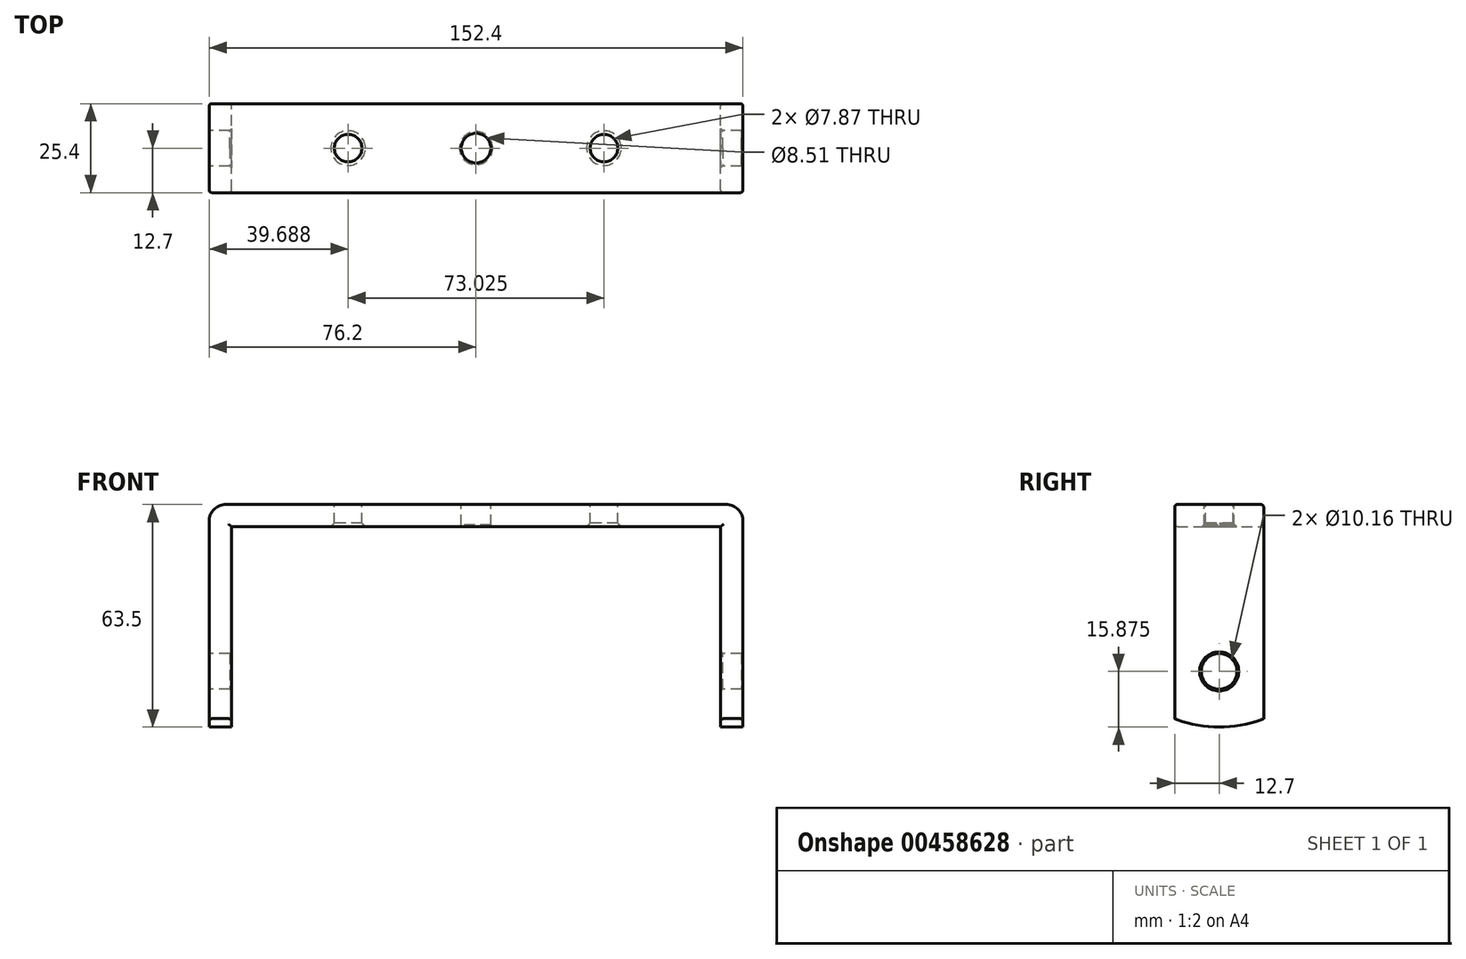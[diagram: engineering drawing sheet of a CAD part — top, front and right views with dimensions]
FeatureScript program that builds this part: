
annotation { "Feature Type Name" : "Feature", "Feature Type Description" : "" }
export const myFeature = defineFeature(function(context is Context, id is Id, definition is map)
    precondition{}
    {
        {
            var Q0;
            Q0=qCreatedBy(makeId("Front.planeOp"),FACE);
            var sketch = newSketch(context, id + "F0", { "sketchPlane" : qUnion([Q0])});
            skLineSegment(sketch, "E0", {"start": v(-69.85, 0) * mm, "end": v(0, 0) * mm});
            skLineSegment(sketch, "E1", {"start": v(-69.85, 0) * mm, "end": v(-69.85, -57.15) * mm});
            skLineSegment(sketch, "E2", {"start": v(0, 0) * mm, "end": v(0, -18.19) * mm, "construction": true});
            skLineSegment(sketch, "E3", {"start": v(-69.85, -57.15) * mm, "end": v(-76.2, -57.15) * mm});
            skLineSegment(sketch, "E4", {"start": v(-76.2, -57.15) * mm, "end": v(-76.2, 6.35) * mm});
            skLineSegment(sketch, "E5", {"start": v(-76.2, 6.35) * mm, "end": v(0, 6.35) * mm});
            skPoint(sketch, "E6.orphan", {"position": v(-69.85, 6.35) * mm});
            skPoint(sketch, "E7.orphan", {"position": v(-76.2, 0) * mm});
            skLineSegment(sketch, "E8.MirrorCS", {"start": v(-69.85, 12.7) * mm, "end": v(0, 12.7) * mm});
            skLineSegment(sketch, "E9.MirrorCS", {"start": v(76.2, 6.35) * mm, "end": v(0, 6.35) * mm});
            skLineSegment(sketch, "E10.MirrorCS", {"start": v(69.85, 0) * mm, "end": v(0, 0) * mm});
            skLineSegment(sketch, "E11.MirrorCS", {"start": v(69.85, 0) * mm, "end": v(69.85, -57.15) * mm});
            skLineSegment(sketch, "E12.MirrorCS", {"start": v(69.85, -57.15) * mm, "end": v(76.2, -57.15) * mm});
            skLineSegment(sketch, "E13.MirrorCS", {"start": v(76.2, -57.15) * mm, "end": v(76.2, 6.35) * mm});
            skSolve(sketch);
        }
        {
            var Q0;
            Q0=makeQuery(id+"F0.imprint","IMPRINT",FACE,{"disambiguationData":[TD([[makeQuery(id+"F0.imprint","IMPRINT",EDGE,{"derivedFrom":sQuery(id+"F0.wireOp",EDGE,"E0")}),1.0]])]});
            extrude(context, id + "F1", {"entities" : qUnion([Q0]), "depth" : 25.4 * mm});
        }
        {
            var Q0;
            Q0=makeQuery(id+"F1.opExtrude","SWEPT_FACE",FACE,{"disambiguationData":[OSD([sQuery(id+"F0.wireOp",EDGE,"E4")])]});
            var sketch = newSketch(context, id + "F2", { "sketchPlane" : qUnion([Q0])});
            skLineSegment(sketch, "E14.0", {"start": v(25.4, 0) * mm, "end": v(0, 0) * mm});
            skCircle(sketch, "E15", {"center": v(12.7, -41.28) * mm, "radius": 5.08 * mm});
            skPoint(sketch, "E15.centerSnap0", {"position": v(12.7, 0) * mm});
            skArc(sketch, "E16", {"start": v(0, -54.76) * mm, "mid": v(12.7, -57.15) * mm, "end": v(25.4, -54.76) * mm});
            skPoint(sketch, "E16.centerSnap0", {"position": v(12.7, -57.15) * mm});
            skLineSegment(sketch, "E17.0", {"start": v(25.4, -57.15) * mm, "end": v(25.4, -54.76) * mm});
            skLineSegment(sketch, "E17.1", {"start": v(25.4, -57.15) * mm, "end": v(0, -57.15) * mm});
            skLineSegment(sketch, "E17.2", {"start": v(0, -57.15) * mm, "end": v(0, -54.76) * mm});
            skLineSegment(sketch, "E18.trimOffspring", {"start": v(0, 0) * mm, "end": v(0, 6.35) * mm});
            skLineSegment(sketch, "E19.trimOffspring", {"start": v(25.4, 0) * mm, "end": v(25.4, 6.35) * mm});
            skSolve(sketch);
        }
        {
            var Q0;
            Q0 = qSketchRegion(id + "F2", true);
            extrude(context, id + "F3", {"entities" : qUnion([Q0]), "operationType" : NewBodyOperationType.REMOVE, "endBound" : BoundingType.THROUGH_ALL, "oppositeDirection" : true, "depth" : 25.4 * mm});
        }
        {
            var Q0;
            Q0=makeQuery(id+"F1.opExtrude","SWEPT_FACE",FACE,{"disambiguationData":[OSD([sQuery(id+"F0.wireOp",EDGE,"E5"),sQuery(id+"F0.wireOp",EDGE,"E9.MirrorCS")])]});
            var sketch = newSketch(context, id + "F4", { "sketchPlane" : qUnion([Q0])});
            skLineSegment(sketch, "E20.0", {"start": v(76.2, 0) * mm, "end": v(-76.2, 0) * mm, "construction": true});
            skLineSegment(sketch, "E20.1", {"start": v(-76.2, -25.4) * mm, "end": v(-76.2, 0) * mm, "construction": true});
            skLineSegment(sketch, "E20.2", {"start": v(76.2, -25.4) * mm, "end": v(-76.2, -25.4) * mm, "construction": true});
            skLineSegment(sketch, "E20.3", {"start": v(76.2, -25.4) * mm, "end": v(76.2, 0) * mm, "construction": true});
            skCircle(sketch, "E21", {"center": v(-36.51, -12.7) * mm, "radius": 3.94 * mm});
            skPoint(sketch, "E21.centerSnap0", {"position": v(-76.2, -12.7) * mm});
            skCircle(sketch, "E22", {"center": v(0, -12.7) * mm, "radius": 4.25 * mm});
            skLineSegment(sketch, "E23", {"start": v(0, 0) * mm, "end": v(0, -25.4) * mm, "construction": true});
            skCircle(sketch, "E24.MirrorC", {"center": v(36.51, -12.7) * mm, "radius": 3.94 * mm});
            skSolve(sketch);
        }
        {
            var Q0;
            Q0 = qSketchRegion(id + "F4", true);
            extrude(context, id + "F5", {"entities" : qUnion([Q0]), "operationType" : NewBodyOperationType.REMOVE, "endBound" : BoundingType.THROUGH_ALL, "oppositeDirection" : true, "depth" : 25.4 * mm});
        }
        {
            var Q0;
            Q0=makeQuery(id+"F5.boolean.opBoolean","COPY",EDGE,{"derivedFrom":makeQuery(id+"F5.opExtrude","CAP_EDGE",EDGE,{"disambiguationData":[OSD([sQuery(id+"F4.wireOp",EDGE,"E21")])],"isStart":true})});
            var Q1;
            Q1=makeQuery(id+"F5.boolean.opBoolean","COPY",EDGE,{"derivedFrom":makeQuery(id+"F5.opExtrude","CAP_EDGE",EDGE,{"disambiguationData":[OSD([sQuery(id+"F4.wireOp",EDGE,"E24.MirrorC")])],"isStart":true})});
            var Q2;
            Q2=makeQuery(id+"F5.boolean.opBoolean","INTERSECT",EDGE,{"derivedFrom":[makeQuery(id+"F1.opExtrude","SWEPT_FACE",FACE,{"disambiguationData":[OSD([sQuery(id+"F0.wireOp",EDGE,"E0"),sQuery(id+"F0.wireOp",EDGE,"E10.MirrorCS")])]}),makeQuery(id+"F5.opExtrude","SWEPT_FACE",FACE,{"disambiguationData":[OSD([sQuery(id+"F4.wireOp",EDGE,"E24.MirrorC")])]})]});
            var Q3;
            Q3=makeQuery(id+"F5.boolean.opBoolean","INTERSECT",EDGE,{"derivedFrom":[makeQuery(id+"F1.opExtrude","SWEPT_FACE",FACE,{"disambiguationData":[OSD([sQuery(id+"F0.wireOp",EDGE,"E0"),sQuery(id+"F0.wireOp",EDGE,"E10.MirrorCS")])]}),makeQuery(id+"F5.opExtrude","SWEPT_FACE",FACE,{"disambiguationData":[OSD([sQuery(id+"F4.wireOp",EDGE,"E21")])]})]});
            chamfer(context, id + "F6", {"entities" : qUnion([Q0, Q1, Q2, Q3]), "width" : 1.02 * mm, "tangentPropagation" : true});
        }
        {
            var Q0;
            Q0=makeQuery(id+"F5.boolean.opBoolean","COPY",EDGE,{"derivedFrom":makeQuery(id+"F5.opExtrude","CAP_EDGE",EDGE,{"disambiguationData":[OSD([sQuery(id+"F4.wireOp",EDGE,"E22")])],"isStart":true})});
            var Q1;
            Q1=makeQuery(id+"F5.boolean.opBoolean","INTERSECT",EDGE,{"derivedFrom":[makeQuery(id+"F1.opExtrude","SWEPT_FACE",FACE,{"disambiguationData":[OSD([sQuery(id+"F0.wireOp",EDGE,"E0"),sQuery(id+"F0.wireOp",EDGE,"E10.MirrorCS")])]}),makeQuery(id+"F5.opExtrude","SWEPT_FACE",FACE,{"disambiguationData":[OSD([sQuery(id+"F4.wireOp",EDGE,"E22")])]})]});
            var Q2;
            Q2=makeQuery(id+"F3.boolean.opBoolean","INTERSECT",EDGE,{"derivedFrom":[makeQuery(id+"F1.opExtrude","SWEPT_FACE",FACE,{"disambiguationData":[OSD([sQuery(id+"F0.wireOp",EDGE,"E1")])]}),makeQuery(id+"F3.opExtrude","SWEPT_FACE",FACE,{"disambiguationData":[OSD([sQuery(id+"F2.wireOp",EDGE,"E15")])]})]});
            var Q3;
            Q3=makeQuery(id+"F3.boolean.opBoolean","INTERSECT",EDGE,{"derivedFrom":[makeQuery(id+"F1.opExtrude","SWEPT_FACE",FACE,{"disambiguationData":[OSD([sQuery(id+"F0.wireOp",EDGE,"E11.MirrorCS")])]}),makeQuery(id+"F3.opExtrude","SWEPT_FACE",FACE,{"disambiguationData":[OSD([sQuery(id+"F2.wireOp",EDGE,"E15")])]})]});
            var Q4;
            Q4=makeQuery(id+"F3.boolean.opBoolean","INTERSECT",EDGE,{"derivedFrom":[makeQuery(id+"F1.opExtrude","SWEPT_FACE",FACE,{"disambiguationData":[OSD([sQuery(id+"F0.wireOp",EDGE,"E13.MirrorCS")])]}),makeQuery(id+"F3.opExtrude","SWEPT_FACE",FACE,{"disambiguationData":[OSD([sQuery(id+"F2.wireOp",EDGE,"E15")])]})]});
            var Q5;
            Q5=makeQuery(id+"F3.boolean.opBoolean","COPY",EDGE,{"derivedFrom":makeQuery(id+"F3.opExtrude","CAP_EDGE",EDGE,{"disambiguationData":[OSD([sQuery(id+"F2.wireOp",EDGE,"E15")])],"isStart":true})});
            chamfer(context, id + "F7", {"entities" : qUnion([Q0, Q1, Q2, Q3, Q4, Q5]), "width" : 0.5 * mm, "tangentPropagation" : true});
        }
        {
            var Q0;
            Q0=makeQuery(id+"F1.opExtrude","SWEPT_EDGE",EDGE,{"disambiguationData":[OSD([sQuery(id+"F0.wireOp",EDGE,"E4"),sQuery(id+"F0.wireOp",EDGE,"E5")])]});
            var Q1;
            Q1=makeQuery(id+"F1.opExtrude","SWEPT_EDGE",EDGE,{"disambiguationData":[OSD([sQuery(id+"F0.wireOp",EDGE,"E9.MirrorCS"),sQuery(id+"F0.wireOp",EDGE,"E13.MirrorCS")])]});
            fillet(context, id + "F8", {"entities" : qUnion([Q0, Q1]), "radius" : 4.83 * mm, "tangentPropagation" : true, "allowEdgeOverflow" : false});
        }
        {
            var Q0;
            Q0=makeQuery(id+"F1.opExtrude","CAP_EDGE",EDGE,{"disambiguationData":[OSD([sQuery(id+"F0.wireOp",EDGE,"E5"),sQuery(id+"F0.wireOp",EDGE,"E9.MirrorCS")])],"isStart":false});
            var Q1;
            {var subQ0=sQuery(id+"F0.wireOp",EDGE,"E4");var subQ1=sQuery(id+"F0.wireOp",EDGE,"E1");var subQ2=sQuery(id+"F2.wireOp",EDGE,"E16");var subQ4=sQuery(id+"F2.wireOp",EDGE,"E17.0");Q1=makeQuery(id+"F3.boolean.opBoolean","COPY",EDGE,{"disambiguationData":[TD([makeQuery(id+"F1.opExtrude","SWEPT_FACE",FACE,{"disambiguationData":[OSD([subQ1])]})])],"derivedFrom":makeQuery(id+"F3.opExtrude","SWEPT_EDGE",EDGE,{"disambiguationData":[OSD([subQ0,subQ2,subQ4])]})});}
            var Q2;
            Q2=makeQuery(id+"F1.opExtrude","CAP_EDGE",EDGE,{"disambiguationData":[OSD([sQuery(id+"F0.wireOp",EDGE,"E1")])],"isStart":false});
            var Q3;
            Q3=makeQuery(id+"F1.opExtrude","CAP_EDGE",EDGE,{"disambiguationData":[OSD([sQuery(id+"F0.wireOp",EDGE,"E0"),sQuery(id+"F0.wireOp",EDGE,"E10.MirrorCS")])],"isStart":false});
            var Q4;
            Q4=makeQuery(id+"F1.opExtrude","CAP_EDGE",EDGE,{"disambiguationData":[OSD([sQuery(id+"F0.wireOp",EDGE,"E11.MirrorCS")])],"isStart":false});
            var Q5;
            {var subQ1=sQuery(id+"F0.wireOp",EDGE,"E11.MirrorCS");var subQ2=sQuery(id+"F2.wireOp",EDGE,"E17.0");var subQ3=sQuery(id+"F2.wireOp",EDGE,"E16");var subQ4=sQuery(id+"F0.wireOp",EDGE,"E4");Q5=makeQuery(id+"F3.boolean.opBoolean","COPY",EDGE,{"disambiguationData":[TD([makeQuery(id+"F1.opExtrude","SWEPT_FACE",FACE,{"disambiguationData":[OSD([subQ1])]})])],"derivedFrom":makeQuery(id+"F3.opExtrude","SWEPT_EDGE",EDGE,{"disambiguationData":[OSD([subQ4,subQ3,subQ2])]})});}
            var Q6;
            Q6=makeQuery(id+"F1.opExtrude","CAP_EDGE",EDGE,{"disambiguationData":[OSD([sQuery(id+"F0.wireOp",EDGE,"E5"),sQuery(id+"F0.wireOp",EDGE,"E9.MirrorCS")])],"isStart":true});
            var Q7;
            Q7=makeQuery(id+"F1.opExtrude","CAP_EDGE",EDGE,{"disambiguationData":[OSD([sQuery(id+"F0.wireOp",EDGE,"E11.MirrorCS")])],"isStart":true});
            var Q8;
            Q8=makeQuery(id+"F1.opExtrude","CAP_EDGE",EDGE,{"disambiguationData":[OSD([sQuery(id+"F0.wireOp",EDGE,"E0"),sQuery(id+"F0.wireOp",EDGE,"E10.MirrorCS")])],"isStart":true});
            var Q9;
            Q9=makeQuery(id+"F1.opExtrude","CAP_EDGE",EDGE,{"disambiguationData":[OSD([sQuery(id+"F0.wireOp",EDGE,"E1")])],"isStart":true});
            var Q10;
            {var subQ0=sQuery(id+"F2.wireOp",EDGE,"E17.2");var subQ1=sQuery(id+"F2.wireOp",EDGE,"E16");var subQ2=sQuery(id+"F0.wireOp",EDGE,"E4");var subQ5=sQuery(id+"F0.wireOp",EDGE,"E11.MirrorCS");Q10=makeQuery(id+"F3.boolean.opBoolean","COPY",EDGE,{"disambiguationData":[TD([makeQuery(id+"F1.opExtrude","SWEPT_FACE",FACE,{"disambiguationData":[OSD([subQ5])]})])],"derivedFrom":makeQuery(id+"F3.opExtrude","SWEPT_EDGE",EDGE,{"disambiguationData":[OSD([subQ2,subQ1,subQ0])]})});}
            var Q11;
            {var subQ0=sQuery(id+"F2.wireOp",EDGE,"E17.2");var subQ1=sQuery(id+"F2.wireOp",EDGE,"E16");var subQ2=sQuery(id+"F0.wireOp",EDGE,"E4");var subQ4=sQuery(id+"F0.wireOp",EDGE,"E1");Q11=makeQuery(id+"F3.boolean.opBoolean","COPY",EDGE,{"disambiguationData":[TD([makeQuery(id+"F1.opExtrude","SWEPT_FACE",FACE,{"disambiguationData":[OSD([subQ4])]})])],"derivedFrom":makeQuery(id+"F3.opExtrude","SWEPT_EDGE",EDGE,{"disambiguationData":[OSD([subQ2,subQ1,subQ0])]})});}
            fillet(context, id + "F9", {"entities" : qUnion([Q0, Q1, Q2, Q3, Q4, Q5, Q6, Q7, Q8, Q9, Q10, Q11]), "radius" : 0.76 * mm, "tangentPropagation" : true, "allowEdgeOverflow" : false});
        }
    });
